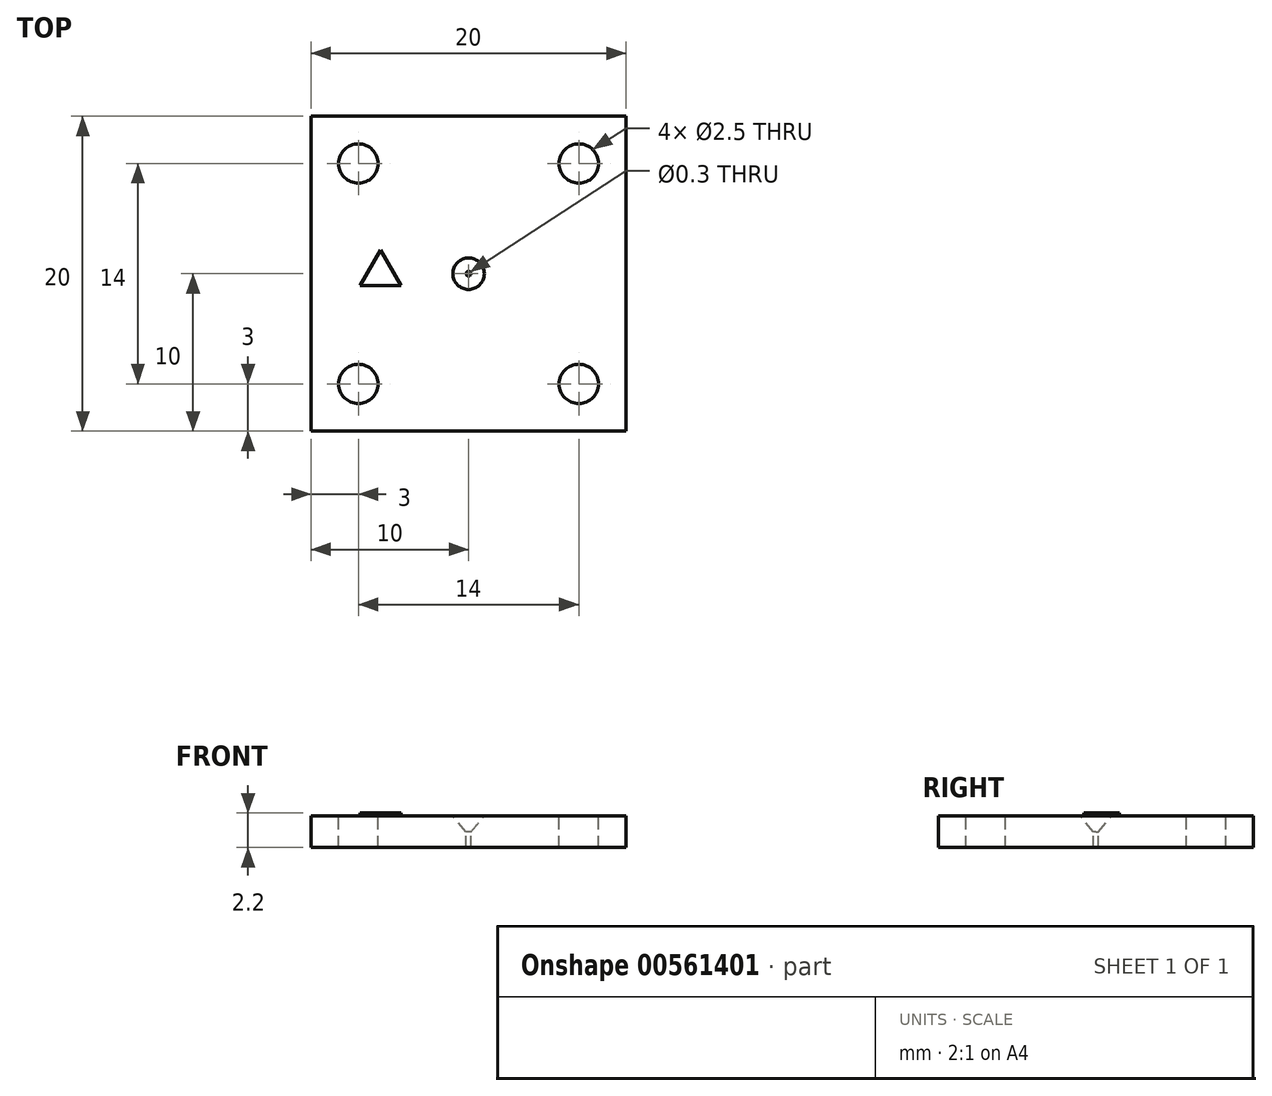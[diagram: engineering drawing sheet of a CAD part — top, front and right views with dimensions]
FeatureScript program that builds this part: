
annotation { "Feature Type Name" : "Feature", "Feature Type Description" : "" }
export const myFeature = defineFeature(function(context is Context, id is Id, definition is map)
    precondition{}
    {
        {
            var Q0;
            Q0=qCreatedBy(makeId("Top.planeOp"),FACE);
            var sketch = newSketch(context, id + "F0", { "sketchPlane" : qUnion([Q0])});
            skLineSegment(sketch, "E0.bottom", {"start": v(-10, 10) * mm, "end": v(10, 10) * mm});
            skLineSegment(sketch, "E0.top", {"start": v(-10, -10) * mm, "end": v(10, -10) * mm});
            skLineSegment(sketch, "E0.left", {"start": v(-10, 10) * mm, "end": v(-10, -10) * mm});
            skLineSegment(sketch, "E0.right", {"start": v(10, 10) * mm, "end": v(10, -10) * mm});
            skSolve(sketch);
        }
        {
            var Q0;
            Q0=makeQuery(id+"F0.imprint","IMPRINT",FACE,{"disambiguationData":[TD([[makeQuery(id+"F0.imprint","IMPRINT",EDGE,{"derivedFrom":sQuery(id+"F0.wireOp",EDGE,"E0.bottom")}),-1.0]])]});
            extrude(context, id + "F1", {"entities" : qUnion([Q0]), "oppositeDirection" : true, "depth" : 1 * mm});
        }
        {
            var Q0;
            Q0=makeQuery(id+"F1.opExtrude","CAP_FACE",FACE,{"disambiguationData":[OSD([sQuery(id+"F0.wireOp",EDGE,"E0.bottom"),sQuery(id+"F0.wireOp",EDGE,"E0.top"),sQuery(id+"F0.wireOp",EDGE,"E0.left"),sQuery(id+"F0.wireOp",EDGE,"E0.right")])],"isStart":true});
            var sketch = newSketch(context, id + "F2", { "sketchPlane" : qUnion([Q0])});
            skCircle(sketch, "E1", {"center": v(0, 0) * mm, "radius": 1 * mm});
            skSolve(sketch);
        }
        {
            var Q0;
            Q0=makeQuery(id+"F1.opExtrude","CAP_FACE",FACE,{"disambiguationData":[OSD([sQuery(id+"F0.wireOp",EDGE,"E0.bottom"),sQuery(id+"F0.wireOp",EDGE,"E0.top"),sQuery(id+"F0.wireOp",EDGE,"E0.left"),sQuery(id+"F0.wireOp",EDGE,"E0.right")])],"isStart":false});
            var sketch = newSketch(context, id + "F3", { "sketchPlane" : qUnion([Q0])});
            skCircle(sketch, "E2", {"center": v(0, 0) * mm, "radius": 0.15 * mm});
            skSolve(sketch);
        }
        {
            var Q1;
            Q1=makeQuery(id+"F2.imprint","IMPRINT",FACE,{"disambiguationData":[TD([[makeQuery(id+"F2.imprint","IMPRINT",EDGE,{"derivedFrom":sQuery(id+"F2.wireOp",EDGE,"E1")}),1.0]])]});
            var Q2;
            Q2=makeQuery(id+"F3.imprint","IMPRINT",FACE,{"disambiguationData":[TD([[makeQuery(id+"F3.imprint","IMPRINT",EDGE,{"derivedFrom":sQuery(id+"F3.wireOp",EDGE,"E2")}),1.0]])]});
            loft(context, id + "F4", {"operationType" : NewBodyOperationType.REMOVE, "sheetProfilesArray" : [{ "sheetProfileEntities" : qUnion([Q1]) }, { "sheetProfileEntities" : qUnion([Q2]) }]});
        }
        {
            var Q0;
            Q0=makeQuery(id+"F2.imprint","IMPRINT",FACE,{"disambiguationData":[TD([[makeQuery(id+"F2.imprint","IMPRINT",EDGE,{"derivedFrom":sQuery(id+"F2.wireOp",EDGE,"E1")}),-1.0]])]});
            var sketch = newSketch(context, id + "F5", { "sketchPlane" : qUnion([Q0])});
            skPoint(sketch, "E3", {"position": v(7, 7) * mm});
            skLineSegment(sketch, "E4", {"start": v(10.77, 0) * mm, "end": v(-10.68, 0) * mm});
            skLineSegment(sketch, "E5", {"start": v(0, -10.66) * mm, "end": v(0, 12.03) * mm});
            skPoint(sketch, "E6.MirrorP", {"position": v(-7, 7) * mm});
            skPoint(sketch, "E7.MirrorP", {"position": v(-7, -7) * mm});
            skPoint(sketch, "E8.MirrorP", {"position": v(7, -7) * mm});
            skSolve(sketch);
        }
        {
            var Q0;
            Q0=makeQuery(id+"F3.imprint","IMPRINT",FACE,{"disambiguationData":[TD([[makeQuery(id+"F3.imprint","IMPRINT",EDGE,{"derivedFrom":sQuery(id+"F3.wireOp",EDGE,"E2")}),-1.0]])]});
            var sketch = newSketch(context, id + "F6", { "sketchPlane" : qUnion([Q0])});
            skLineSegment(sketch, "E9.bottom", {"start": v(-10, 10) * mm, "end": v(10, 10) * mm});
            skLineSegment(sketch, "E9.top", {"start": v(-10, -10) * mm, "end": v(10, -10) * mm});
            skLineSegment(sketch, "E9.left", {"start": v(-10, 10) * mm, "end": v(-10, -10) * mm});
            skLineSegment(sketch, "E9.right", {"start": v(10, 10) * mm, "end": v(10, -10) * mm});
            skPoint(sketch, "E9.middle", {"position": v(0, 0) * mm});
            skCircle(sketch, "E10.0", {"center": v(0, 0) * mm, "radius": 0.15 * mm});
            skSolve(sketch);
        }
        {
            var Q0;
            Q0=makeQuery(id+"F6.imprint","IMPRINT",FACE,{"disambiguationData":[TD([[makeQuery(id+"F6.imprint","IMPRINT",EDGE,{"derivedFrom":sQuery(id+"F6.wireOp",EDGE,"E9.bottom")}),-1.0]])]});
            extrude(context, id + "F7", {"entities" : qUnion([Q0]), "operationType" : NewBodyOperationType.ADD, "depth" : 1 * mm});
        }
        {
            var Q0;
            Q0=sQuery(id+"F5.wireOp",VERTEX,"E7.MirrorP");
            var Q1;
            Q1=sQuery(id+"F5.wireOp",VERTEX,"E8.MirrorP");
            var Q2;
            Q2=sQuery(id+"F5.wireOp",VERTEX,"E3");
            var Q3;
            Q3=sQuery(id+"F5.wireOp",VERTEX,"E6.MirrorP");
            var Q4;
            Q4=makeQuery(id+"F1.opExtrude","SWEPT_BODY",BODY,{"disambiguationData":[OSD([sQuery(id+"F0.wireOp",EDGE,"E0.bottom"),sQuery(id+"F0.wireOp",EDGE,"E0.top"),sQuery(id+"F0.wireOp",EDGE,"E0.left"),sQuery(id+"F0.wireOp",EDGE,"E0.right")])]});
            hole(context, id + "F8", {"style" : HoleStyle.SIMPLE, "endStyle" : HoleEndStyle.THROUGH, "standardTappedOrClearance" : lookupTablePath({ "standard" : "ISO", "engagement" : "75%", "pitch" : "0.5 mm", "size" : "M3", "type" : "Tapped" }), "standardBlindInLast" : lookupTablePath({ "standard" : "ISO", "engagement" : "75%", "pitch" : "0.5 mm", "size" : "M3", "type" : "Tapped" }), "holeDiameter" : 2.5 * mm, "showTappedDepth" : true, "isTappedThrough" : true, "tappedDepth" : 12 * mm, "tapClearance" : 3, "startFromSketch" : true, "locations" : qUnion([Q0, Q1, Q2, Q3]), "scope" : qUnion([Q4]), "majorDiameter" : 3 * mm});
        }
        {
            var Q0;
            Q0=makeQuery(id+"F2.imprint","IMPRINT",FACE,{"disambiguationData":[TD([[makeQuery(id+"F2.imprint","IMPRINT",EDGE,{"derivedFrom":sQuery(id+"F2.wireOp",EDGE,"E1")}),-1.0]])]});
            var sketch = newSketch(context, id + "F9", { "sketchPlane" : qUnion([Q0])});
            skCircle(sketch, "E11.cCircle", {"center": v(-5.6, 0) * mm, "radius": 1.5 * mm, "construction": true});
            skLineSegment(sketch, "E11.0", {"start": v(-5.6, 1.5) * mm, "end": v(-4.3, -0.75) * mm});
            skLineSegment(sketch, "E11.1", {"start": v(-4.3, -0.75) * mm, "end": v(-6.9, -0.75) * mm});
            skLineSegment(sketch, "E11.2", {"start": v(-6.9, -0.75) * mm, "end": v(-5.6, 1.5) * mm});
            skSolve(sketch);
        }
        {
            var Q0;
            Q0=qSketchRegion(id+"F9",true);
            extrude(context, id + "F10", {"entities" : qUnion([Q0]), "operationType" : NewBodyOperationType.ADD, "depth" : .2 * mm, "offsetDistance" : 25 * mm});
        }
    });
